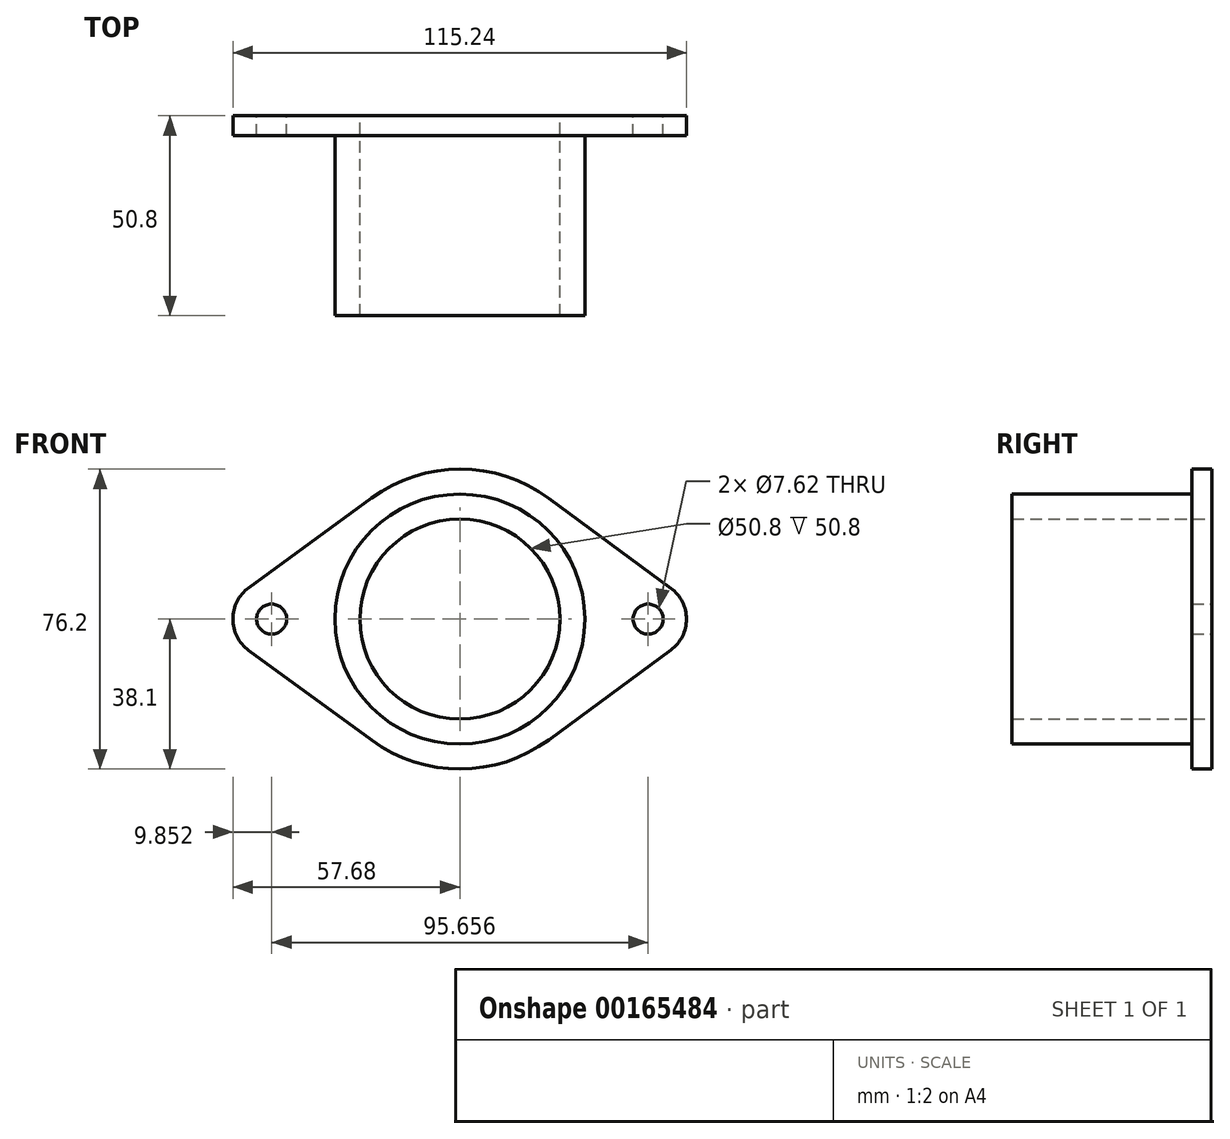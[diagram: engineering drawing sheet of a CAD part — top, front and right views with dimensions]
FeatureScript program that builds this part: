
annotation { "Feature Type Name" : "Feature", "Feature Type Description" : "" }
export const myFeature = defineFeature(function(context is Context, id is Id, definition is map)
    precondition{}
    {
        {
            var Q0;
            Q0=qCreatedBy(makeId("Front.planeOp"),FACE);
            var sketch = newSketch(context, id + "F0", { "sketchPlane" : qUnion([Q0])});
            skCircle(sketch, "E0", {"center": v(0, 0) * mm, "radius": 31.75 * mm});
            skCircle(sketch, "E1", {"center": v(0, 0) * mm, "radius": 25.4 * mm});
            skLineSegment(sketch, "E2", {"start": v(-83.32, 0) * mm, "end": v(108.92, 0) * mm, "construction": true});
            skArc(sketch, "E3", {"start": v(-53.65, 7.95) * mm, "mid": v(-57.68, 0) * mm, "end": v(-53.65, -7.95) * mm});
            skCircle(sketch, "E4", {"center": v(47.83, 0) * mm, "radius": 9.73 * mm});
            skCircle(sketch, "E5", {"center": v(-47.83, 0) * mm, "radius": 3.81 * mm});
            skCircle(sketch, "E6", {"center": v(47.83, 0) * mm, "radius": 3.81 * mm});
            skLineSegment(sketch, "E7", {"start": v(-53.65, 7.95) * mm, "end": v(-22.5, 30.75) * mm});
            skLineSegment(sketch, "E8", {"start": v(22.6, 30.67) * mm, "end": v(53.6, 7.83) * mm});
            skLineSegment(sketch, "E9", {"start": v(22.6, -30.67) * mm, "end": v(53.6, -7.83) * mm});
            skLineSegment(sketch, "E10", {"start": v(-53.65, -7.95) * mm, "end": v(-22.5, -30.75) * mm});
            skArc(sketch, "E11.trimOffspring", {"start": v(-22.5, -30.75) * mm, "mid": v(0.06, -38.1) * mm, "end": v(22.6, -30.67) * mm});
            skArc(sketch, "E12.trimOffspring", {"start": v(22.6, 30.67) * mm, "mid": v(0.06, 38.1) * mm, "end": v(-22.5, 30.75) * mm});
            skSolve(sketch);
        }
        {
            var Q0;
            Q0=makeQuery(id+"F0.imprint","IMPRINT",FACE,{"disambiguationData":[TD([[makeQuery(id+"F0.imprint","IMPRINT",EDGE,{"derivedFrom":sQuery(id+"F0.wireOp",EDGE,"E0")}),-1.0]])]});
            var Q1;
            Q1=makeQuery(id+"F0.imprint","IMPRINT",FACE,{"disambiguationData":[TD([[makeQuery(id+"F0.imprint","IMPRINT",EDGE,{"derivedFrom":sQuery(id+"F0.wireOp",EDGE,"E0")}),1.0]])]});
            var Q2;
            Q2=makeQuery(id+"F0.imprint","IMPRINT",FACE,{"disambiguationData":[TD([[makeQuery(id+"F0.imprint","IMPRINT",EDGE,{"derivedFrom":sQuery(id+"F0.wireOp",EDGE,"E6")}),-1.0]])]});
            extrude(context, id + "F1", {"entities" : qUnion([Q0, Q1, Q2]), "depth" : 5.08 * mm});
        }
        {
            var Q0;
            Q0=makeQuery(id+"F1.opExtrude","CAP_FACE",FACE,{"disambiguationData":[OSD([sQuery(id+"F0.wireOp",EDGE,"E1"),sQuery(id+"F0.wireOp",EDGE,"E3"),sQuery(id+"F0.wireOp",EDGE,"E4"),sQuery(id+"F0.wireOp",EDGE,"E5"),sQuery(id+"F0.wireOp",EDGE,"E6"),sQuery(id+"F0.wireOp",EDGE,"E7"),sQuery(id+"F0.wireOp",EDGE,"E8"),sQuery(id+"F0.wireOp",EDGE,"E9"),sQuery(id+"F0.wireOp",EDGE,"E10"),sQuery(id+"F0.wireOp",EDGE,"E11.trimOffspring"),sQuery(id+"F0.wireOp",EDGE,"E12.trimOffspring")])],"isStart":false});
            var sketch = newSketch(context, id + "F2", { "sketchPlane" : qUnion([Q0])});
            skCircle(sketch, "E13", {"center": v(0, 0) * mm, "radius": 25.4 * mm});
            skCircle(sketch, "E14", {"center": v(0, 0) * mm, "radius": 31.75 * mm});
            skSolve(sketch);
        }
        {
            var Q0;
            Q0 = qSketchRegion(id + "F2", true);
            extrude(context, id + "F3", {"entities" : qUnion([Q0]), "operationType" : NewBodyOperationType.ADD, "depth" : 45.72 * mm});
        }
    });
